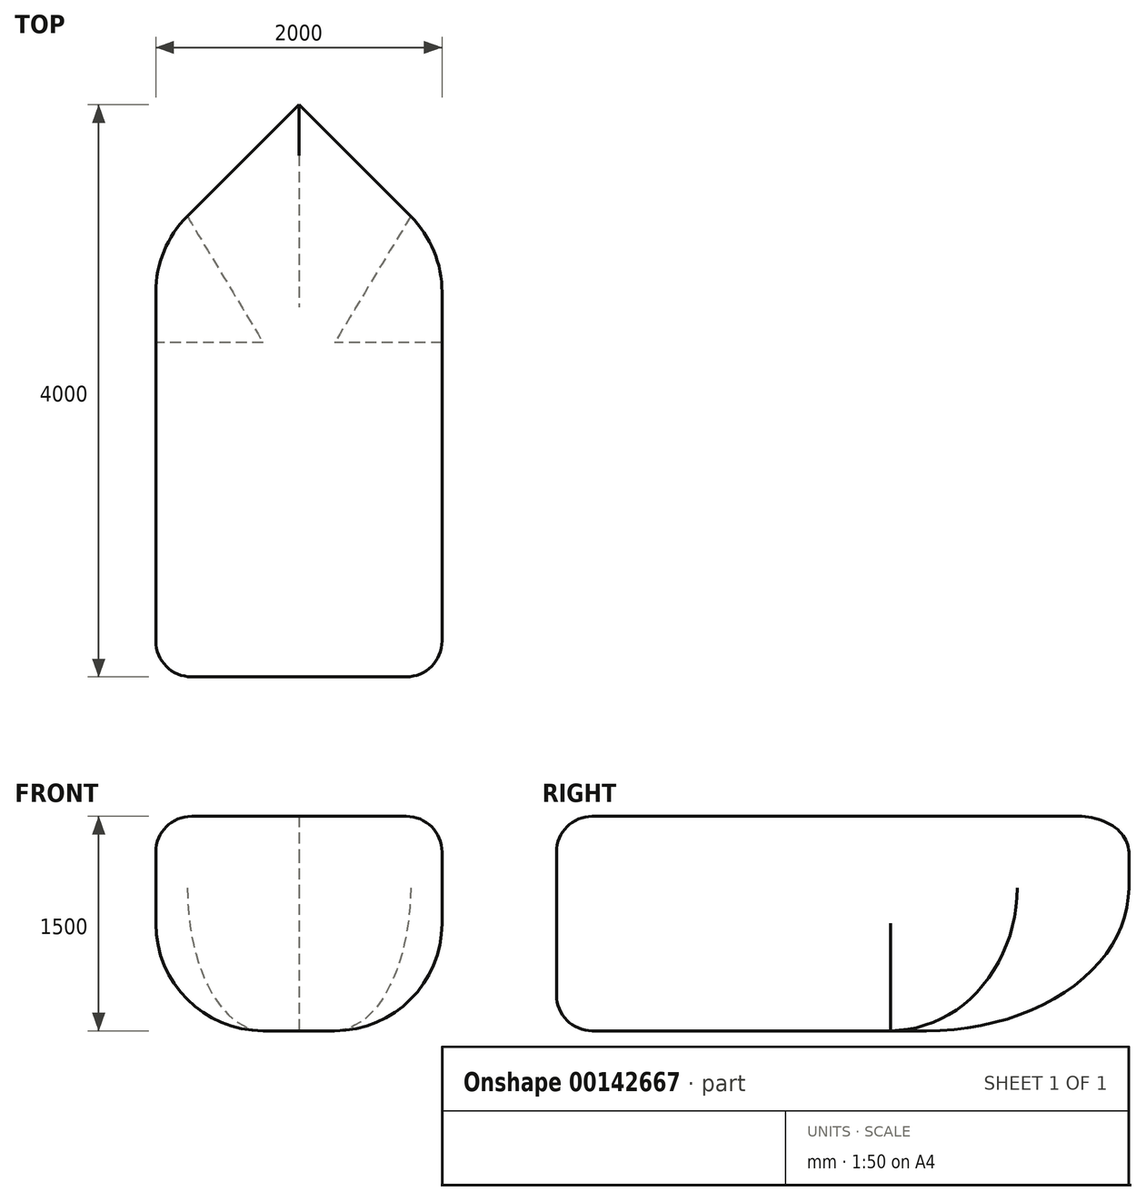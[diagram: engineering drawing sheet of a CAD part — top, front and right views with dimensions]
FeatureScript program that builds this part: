
annotation { "Feature Type Name" : "Feature", "Feature Type Description" : "" }
export const myFeature = defineFeature(function(context is Context, id is Id, definition is map)
    precondition{}
    {
        {
            var Q0;
            Q0=qCreatedBy(makeId("Right.planeOp"),FACE);
            var sketch = newSketch(context, id + "F0", { "sketchPlane" : qUnion([Q0])});
            skLineSegment(sketch, "E0.bottom", {"start": v(-2000, -750) * mm, "end": v(2000, -750) * mm});
            skLineSegment(sketch, "E0.top", {"start": v(-2000, 750) * mm, "end": v(2000, 750) * mm});
            skLineSegment(sketch, "E0.left", {"start": v(-2000, -750) * mm, "end": v(-2000, 750) * mm});
            skLineSegment(sketch, "E0.right", {"start": v(2000, -750) * mm, "end": v(2000, 750) * mm});
            skPoint(sketch, "E0.middle", {"position": v(0, 0) * mm});
            skSolve(sketch);
        }
        {
            var Q0;
            Q0=makeQuery(id+"F0.imprint","IMPRINT",FACE,{"disambiguationData":[TD([[makeQuery(id+"F0.imprint","IMPRINT",EDGE,{"derivedFrom":sQuery(id+"F0.wireOp",EDGE,"E0.bottom")}),1.0]])]});
            extrude(context, id + "F1", {"entities" : qUnion([Q0]), "endBound" : BoundingType.SYMMETRIC, "depth" : 2000 * mm});
        }
        {
            var Q0;
            Q0=makeQuery(id+"F1.opExtrude","CAP_EDGE",EDGE,{"disambiguationData":[OSD([sQuery(id+"F0.wireOp",EDGE,"E0.right")])],"isStart":false});
            var Q1;
            Q1=makeQuery(id+"F1.opExtrude","CAP_EDGE",EDGE,{"disambiguationData":[OSD([sQuery(id+"F0.wireOp",EDGE,"E0.right")])],"isStart":true});
            chamfer(context, id + "F2", {"entities" : qUnion([Q0, Q1]), "width" : 1000 * mm, "tangentPropagation" : true});
        }
        {
            var Q0;
            Q0=makeQuery(id+"F2.opChamfer","BLEND_EDGE",EDGE,{"blendedFrom":[makeQuery(id+"F1.opExtrude","CAP_EDGE",EDGE,{"disambiguationData":[OSD([sQuery(id+"F0.wireOp",EDGE,"E0.right")])],"isStart":false}),makeQuery(id+"F1.opExtrude","SWEPT_FACE",FACE,{"disambiguationData":[OSD([sQuery(id+"F0.wireOp",EDGE,"E0.bottom")])]})],"blendedInto":[makeQuery(id+"F1.opExtrude","SWEPT_FACE",FACE,{"disambiguationData":[OSD([sQuery(id+"F0.wireOp",EDGE,"E0.bottom")])]})]});
            var Q1;
            Q1=makeQuery(id+"F2.opChamfer","BLEND_EDGE",EDGE,{"blendedFrom":[makeQuery(id+"F1.opExtrude","CAP_EDGE",EDGE,{"disambiguationData":[OSD([sQuery(id+"F0.wireOp",EDGE,"E0.right")])],"isStart":true}),makeQuery(id+"F1.opExtrude","SWEPT_FACE",FACE,{"disambiguationData":[OSD([sQuery(id+"F0.wireOp",EDGE,"E0.bottom")])]})],"blendedInto":[makeQuery(id+"F1.opExtrude","SWEPT_FACE",FACE,{"disambiguationData":[OSD([sQuery(id+"F0.wireOp",EDGE,"E0.bottom")])]})]});
            fillet(context, id + "F3", {"entities" : qUnion([Q0, Q1]), "radius" : 1000 * mm, "tangentPropagation" : true, "allowEdgeOverflow" : false});
        }
        {
            var Q0;
            Q0=makeQuery(id+"F1.opExtrude","CAP_EDGE",EDGE,{"disambiguationData":[OSD([sQuery(id+"F0.wireOp",EDGE,"E0.bottom")])],"isStart":false});
            var Q1;
            Q1=makeQuery(id+"F1.opExtrude","CAP_EDGE",EDGE,{"disambiguationData":[OSD([sQuery(id+"F0.wireOp",EDGE,"E0.bottom")])],"isStart":true});
            fillet(context, id + "F4", {"entities" : qUnion([Q0, Q1]), "radius" : 750 * mm, "tangentPropagation" : true, "allowEdgeOverflow" : false});
        }
        {
            var Q0;
            Q0=makeQuery(id+"F1.opExtrude","CAP_EDGE",EDGE,{"disambiguationData":[OSD([sQuery(id+"F0.wireOp",EDGE,"E0.left")])],"isStart":true});
            var Q1;
            Q1=makeQuery(id+"F1.opExtrude","SWEPT_EDGE",EDGE,{"disambiguationData":[OSD([sQuery(id+"F0.wireOp",EDGE,"E0.bottom"),sQuery(id+"F0.wireOp",EDGE,"E0.left")])]});
            var Q2;
            Q2=makeQuery(id+"F1.opExtrude","CAP_EDGE",EDGE,{"disambiguationData":[OSD([sQuery(id+"F0.wireOp",EDGE,"E0.left")])],"isStart":false});
            fillet(context, id + "F5", {"entities" : qUnion([Q0, Q1, Q2]), "radius" : 250 * mm, "tangentPropagation" : true, "allowEdgeOverflow" : false});
        }
        {
            var Q0;
            Q0=makeQuery(id+"F1.opExtrude","SWEPT_FACE",FACE,{"disambiguationData":[OSD([sQuery(id+"F0.wireOp",EDGE,"E0.top")])]});
            fillet(context, id + "F6", {"entities" : qUnion([Q0]), "radius" : 250 * mm, "tangentPropagation" : true, "allowEdgeOverflow" : false});
        }
    });
